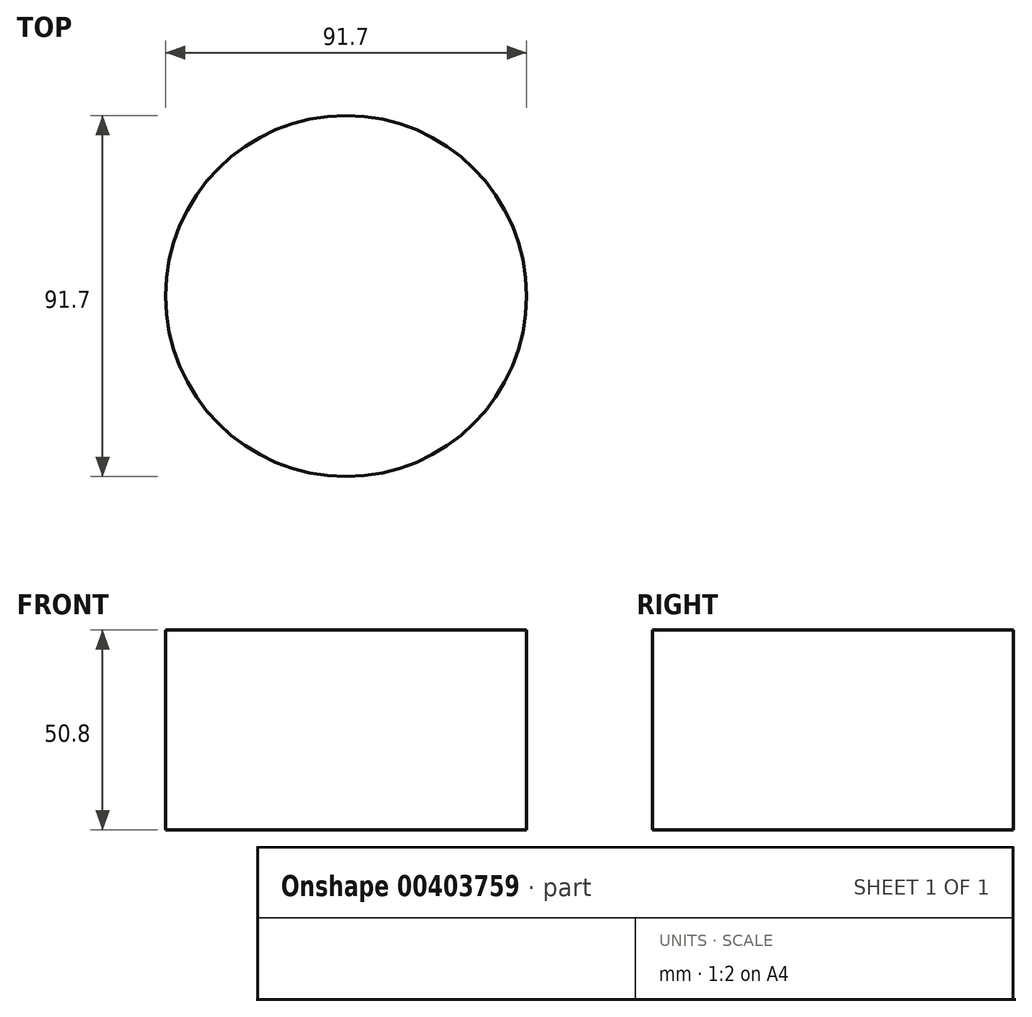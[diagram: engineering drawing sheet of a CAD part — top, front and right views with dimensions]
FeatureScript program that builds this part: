
annotation { "Feature Type Name" : "Feature", "Feature Type Description" : "" }
export const myFeature = defineFeature(function(context is Context, id is Id, definition is map)
    precondition{}
    {
        {
            var Q0;
            Q0=qCreatedBy(makeId("Top.planeOp"),FACE);
            var sketch = newSketch(context, id + "F0", { "sketchPlane" : qUnion([Q0])});
            skCircle(sketch, "E0", {"center": v(0, 0) * mm, "radius": 45.85 * mm});
            skSolve(sketch);
        }
        {
            var Q0;
            Q0 = qSketchRegion(id + "F0", true);
            extrude(context, id + "F1", {"entities" : qUnion([Q0]), "depth" : 50.8 * mm, "offsetDistance" : 25.4 * mm});
        }
    });
